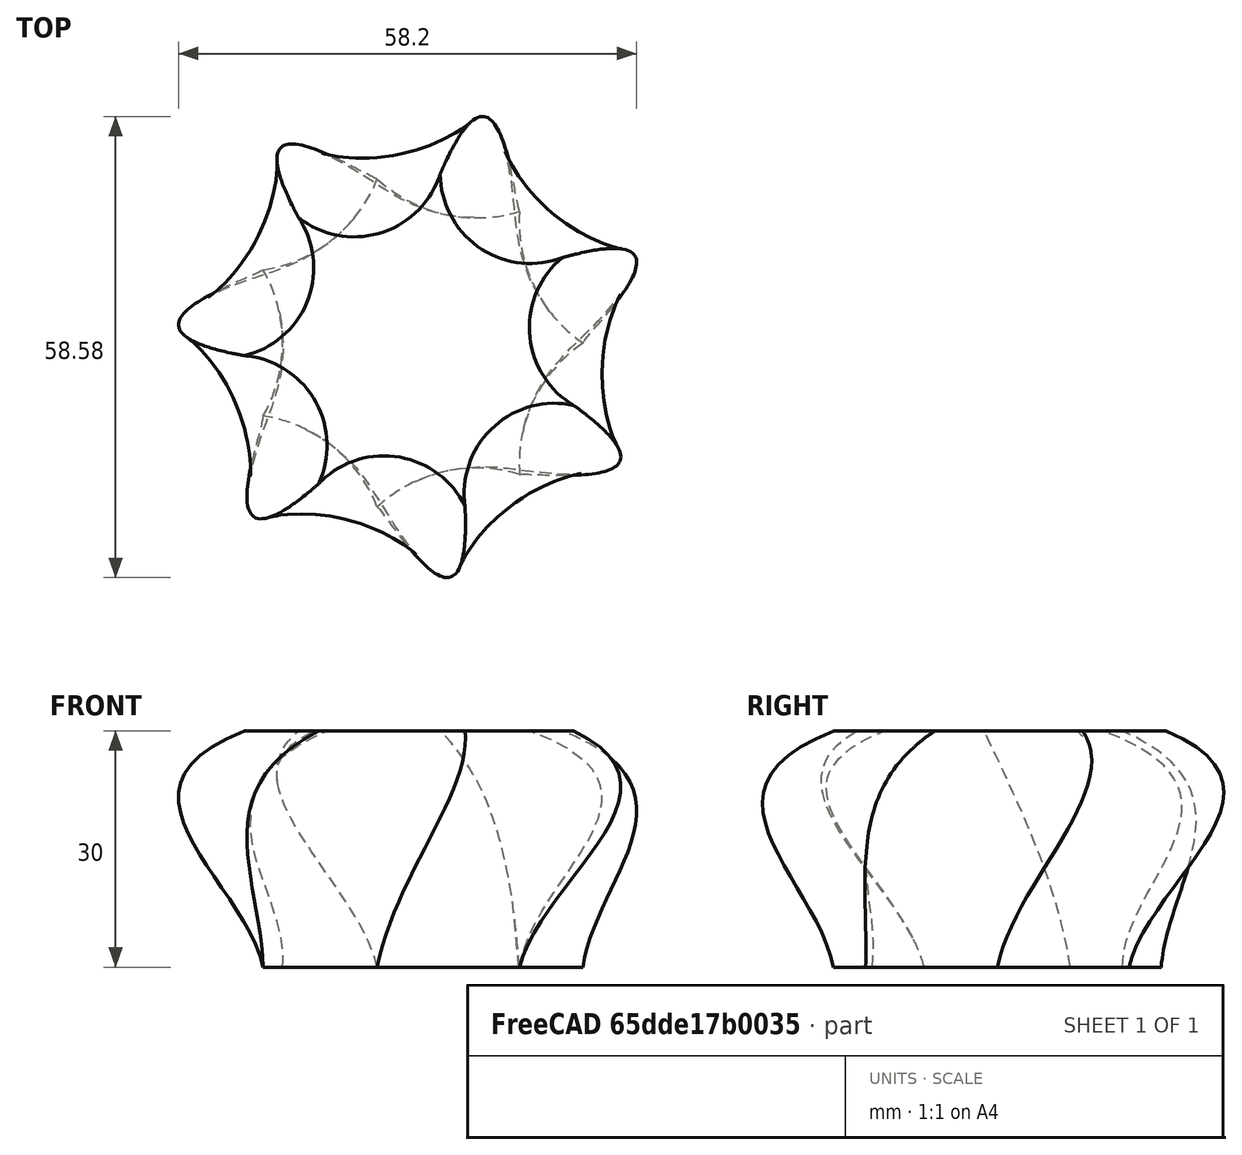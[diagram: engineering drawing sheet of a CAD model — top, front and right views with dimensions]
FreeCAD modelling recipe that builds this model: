
FCSTD DOCUMENT  (FreeCAD 1.2R20251119 (Git shallow))
Label: turned_loft
License: All rights reserved
LicenseURL: https://en.wikipedia.org/wiki/All_rights_reserved
objects: Sketcher::SketchObject×4, App::Point×1, PartDesign::AdditiveLoft×1, PartDesign::Body×1
note: 12 computed .brp shape members not serialized (recipe doc carries the construction recipe); baked Part::Feature solids carry a one-line shape summary decoded from their .brp

FEATURE [App::Point] Origin001
  Role = Origin
FEATURE [Sketcher::SketchObject] Sketch
  ArcFitTolerance = 1e-06
  AttachmentSupport = -> [Origin]
  ExternalTypes = [0]
  FullyConstrained = false
  MakeInternals = false
  MapMode = 5
  sketch-geometry (9):
    g0: ArcOfCircle CenterX=31.9361 CenterY=15.3796 CenterZ=0 NormalX=0 NormalY=0 NormalZ=1 AngleXU=0 Radius=18.6618 StartAngle=3.07054 EndAngle=4.11025
    g1: ArcOfCircle CenterX=31.9361 CenterY=-15.3796 CenterZ=0 NormalX=0 NormalY=0 NormalZ=1 AngleXU=0 Radius=18.6618 StartAngle=2.17294 EndAngle=3.21265
    g2: ArcOfCircle CenterX=7.88755 CenterY=-34.5576 CenterZ=0 NormalX=0 NormalY=0 NormalZ=1 AngleXU=0 Radius=18.6618 StartAngle=1.27534 EndAngle=2.31505
    g3: ArcOfCircle CenterX=-22.1004 CenterY=-27.7131 CenterZ=0 NormalX=0 NormalY=0 NormalZ=1 AngleXU=0 Radius=18.6618 StartAngle=0.377744 EndAngle=1.41745
    g4: ArcOfCircle CenterX=-35.4463 CenterY=2e-15 CenterZ=0 NormalX=0 NormalY=0 NormalZ=1 AngleXU=0 Radius=18.6618 StartAngle=5.76333 EndAngle=6.80304
    g5: ArcOfCircle CenterX=-22.1004 CenterY=27.7131 CenterZ=0 NormalX=0 NormalY=0 NormalZ=1 AngleXU=0 Radius=18.6618 StartAngle=4.86573 EndAngle=5.90544
    g6: ArcOfCircle CenterX=7.88755 CenterY=34.5576 CenterZ=0 NormalX=0 NormalY=0 NormalZ=1 AngleXU=0 Radius=18.6618 StartAngle=3.96814 EndAngle=5.00784
    g7: Circle [constr] CenterX=0 CenterY=0 CenterZ=0 NormalX=0 NormalY=0 NormalZ=1 AngleXU=0 Radius=35.4463
    g8: Circle [constr] CenterX=0 CenterY=0 CenterZ=0 NormalX=0 NormalY=0 NormalZ=1 AngleXU=0 Radius=21.3658
  constraints (30):
    c: Coincident(g3,g2)
    c: Coincident(g0,g6)
    c: Coincident(g7,g-1)
    c: PointOnObject(g6,g7)
    c: Coincident(g5,g6)
    c: PointOnObject(g0,g7)
    c: Coincident(g1,g0)
    c: PointOnObject(g1,g7)
    c: Coincident(g1,g2)
    c: PointOnObject(g2,g7)
    c: Equal(g2,g1)
    c: Equal(g1,g0)
    c: Coincident(g4,g5)
    c: Coincident(g3,g4)
    c: PointOnObject(g3,g7)
    c: PointOnObject(g4,g7)
    c: PointOnObject(g5,g7)
    c: Equal(g6,g5)
    c: Equal(g5,g4)
    c: Equal(g4,g3)
    c: Equal(g3,g2)
    c: Coincident(g8,g7)
    c: PointOnObject(g0,g8)
    c: PointOnObject(g5,g8)
    c: PointOnObject(g4,g8)
    c: PointOnObject(g3,g8)
    c: PointOnObject(g2,g8)
    c: PointOnObject(g1,g8)
    c: PointOnObject(g0,g8)
    c: PointOnObject(g0,g-1)
FEATURE [Sketcher::SketchObject] Sketch001
  ArcFitTolerance = 1e-06
  AttachmentOffset = pos=(0,0,10) rot=(0,0,1;0rad)
  AttachmentSupport = -> [Sketch]
  ExternalTypes = [0]
  FullyConstrained = false
  MakeInternals = false
  MapMode = 2
  Placement = pos=(0,0,10) rot=(0,0,1;0rad)
  sketch-geometry (10):
    g0: ArcOfCircle CenterX=31.7447 CenterY=22.8229 CenterZ=0 NormalX=0 NormalY=0 NormalZ=1 AngleXU=0 Radius=19.6047 StartAngle=3.168 EndAngle=4.36185
    g1: ArcOfCircle CenterX=37.6362 CenterY=-10.5892 CenterZ=0 NormalX=0 NormalY=0 NormalZ=1 AngleXU=0 Radius=19.6047 StartAngle=2.2704 EndAngle=3.46425
    g2: ArcOfCircle CenterX=15.1868 CenterY=-36.0274 CenterZ=0 NormalX=0 NormalY=0 NormalZ=1 AngleXU=0 Radius=19.6047 StartAngle=1.3728 EndAngle=2.56666
    g3: ArcOfCircle CenterX=-18.6985 CenterY=-34.3363 CenterZ=0 NormalX=0 NormalY=0 NormalZ=1 AngleXU=0 Radius=19.6047 StartAngle=0.475203 EndAngle=1.66906
    g4: ArcOfCircle CenterX=-38.5035 CenterY=-6.78921 CenterZ=0 NormalX=0 NormalY=0 NormalZ=1 AngleXU=0 Radius=19.6047 StartAngle=5.86079 EndAngle=7.05465
    g5: ArcOfCircle CenterX=-29.3146 CenterY=25.8703 CenterZ=0 NormalX=0 NormalY=0 NormalZ=1 AngleXU=0 Radius=19.6047 StartAngle=4.96319 EndAngle=6.15705
    g6: ArcOfCircle CenterX=1.94885 CenterY=39.0489 CenterZ=0 NormalX=0 NormalY=0 NormalZ=1 AngleXU=0 Radius=19.6047 StartAngle=4.06559 EndAngle=5.25945
    g7: Circle [constr] CenterX=0 CenterY=0 CenterZ=0 NormalX=0 NormalY=0 NormalZ=1 AngleXU=0 Radius=39.0975
    g8: Circle [constr] CenterX=0 CenterY=0 CenterZ=0 NormalX=0 NormalY=0 NormalZ=1 AngleXU=0 Radius=25.3983
    g9: LineSegment [constr] StartX=0 StartY=0 StartZ=0 EndX=25.0124 EndY=4.41037 EndZ=0
  constraints (32):
    c: Coincident(g3,g2)
    c: Coincident(g0,g6)
    c: Coincident(g7,g-1)
    c: PointOnObject(g6,g7)
    c: Coincident(g5,g6)
    c: PointOnObject(g0,g7)
    c: Coincident(g1,g0)
    c: PointOnObject(g1,g7)
    c: Coincident(g1,g2)
    c: PointOnObject(g2,g7)
    c: Equal(g2,g1)
    c: Equal(g1,g0)
    c: Coincident(g4,g5)
    c: Coincident(g3,g4)
    c: PointOnObject(g3,g7)
    c: PointOnObject(g4,g7)
    c: PointOnObject(g5,g7)
    c: Equal(g6,g5)
    c: Equal(g5,g4)
    c: Equal(g4,g3)
    c: Equal(g3,g2)
    c: Coincident(g8,g7)
    c: PointOnObject(g0,g8)
    c: PointOnObject(g5,g8)
    c: PointOnObject(g4,g8)
    c: PointOnObject(g3,g8)
    c: PointOnObject(g2,g8)
    c: PointOnObject(g1,g8)
    c: PointOnObject(g0,g8)
    c: Coincident(g9,g7)
    c: Coincident(g9,g0)
    c: Angle(g-1,g9) = 0.174533
FEATURE [Sketcher::SketchObject] Sketch002
  ArcFitTolerance = 1e-06
  AttachmentOffset = pos=(0,0,20) rot=(0,0,1;0rad)
  AttachmentSupport = -> [XY_Plane]
  ExternalTypes = [0]
  FullyConstrained = false
  MakeInternals = false
  MapMode = 2
  Placement = pos=(0,0,20) rot=(0,0,1;0rad)
  sketch-geometry (10):
    g0: ArcOfCircle CenterX=36.6006 CenterY=37.5248 CenterZ=0 NormalX=0 NormalY=0 NormalZ=1 AngleXU=0 Radius=28.5333 StartAngle=3.4658 EndAngle=4.41312
    g1: ArcOfCircle CenterX=52.1582 CenterY=-5.21921 CenterZ=0 NormalX=0 NormalY=0 NormalZ=1 AngleXU=0 Radius=28.5333 StartAngle=2.5682 EndAngle=3.51552
    g2: ArcOfCircle CenterX=28.4395 CenterY=-44.033 CenterZ=0 NormalX=0 NormalY=0 NormalZ=1 AngleXU=0 Radius=28.5333 StartAngle=1.6706 EndAngle=2.61792
    g3: ArcOfCircle CenterX=-16.6946 CenterY=-49.6891 CenterZ=0 NormalX=0 NormalY=0 NormalZ=1 AngleXU=0 Radius=28.5333 StartAngle=0.773004 EndAngle=1.72032
    g4: ArcOfCircle CenterX=-49.2574 CenterY=-17.9282 CenterZ=0 NormalX=0 NormalY=0 NormalZ=1 AngleXU=0 Radius=28.5333 StartAngle=6.15859 EndAngle=7.10591
    g5: ArcOfCircle CenterX=-44.7284 CenterY=27.3329 CenterZ=0 NormalX=0 NormalY=0 NormalZ=1 AngleXU=0 Radius=28.5333 StartAngle=5.26099 EndAngle=6.20831
    g6: ArcOfCircle CenterX=-6.51793 CenterY=52.0118 CenterZ=0 NormalX=0 NormalY=0 NormalZ=1 AngleXU=0 Radius=28.5333 StartAngle=4.3634 EndAngle=5.31071
    g7: Circle [constr] CenterX=0 CenterY=0 CenterZ=0 NormalX=0 NormalY=0 NormalZ=1 AngleXU=0 Radius=52.4187
    g8: Circle [constr] CenterX=0 CenterY=0 CenterZ=0 NormalX=0 NormalY=0 NormalZ=1 AngleXU=0 Radius=29.9974
    g9: LineSegment [constr] StartX=0 StartY=0 StartZ=0 EndX=28.1883 EndY=10.2597 EndZ=0
  constraints (32):
    c: Coincident(g3,g2)
    c: Coincident(g0,g6)
    c: Coincident(g7,g-1)
    c: PointOnObject(g6,g7)
    c: Coincident(g5,g6)
    c: PointOnObject(g0,g7)
    c: Coincident(g1,g0)
    c: PointOnObject(g1,g7)
    c: Coincident(g1,g2)
    c: PointOnObject(g2,g7)
    c: Equal(g2,g1)
    c: Equal(g1,g0)
    c: Coincident(g4,g5)
    c: Coincident(g3,g4)
    c: PointOnObject(g3,g7)
    c: PointOnObject(g4,g7)
    c: PointOnObject(g5,g7)
    c: Equal(g6,g5)
    c: Equal(g5,g4)
    c: Equal(g4,g3)
    c: Equal(g3,g2)
    c: Coincident(g8,g7)
    c: PointOnObject(g0,g8)
    c: PointOnObject(g5,g8)
    c: PointOnObject(g4,g8)
    c: PointOnObject(g3,g8)
    c: PointOnObject(g2,g8)
    c: PointOnObject(g1,g8)
    c: PointOnObject(g0,g8)
    c: Coincident(g9,g7)
    c: Coincident(g9,g0)
    c: Angle(g-1,g9) = 0.349066
FEATURE [Sketcher::SketchObject] Sketch003
  ArcFitTolerance = 1e-06
  AttachmentOffset = pos=(0,0,30) rot=(0,0,1;0rad)
  AttachmentSupport = -> [Origin]
  ExternalTypes = [0]
  FullyConstrained = false
  MakeInternals = false
  MapMode = 5
  Placement = pos=(0,0,30) rot=(0,0,1;0rad)
  sketch-geometry (10):
    g0: ArcOfCircle CenterX=14.7064 CenterY=21.5703 CenterZ=0 NormalX=0 NormalY=0 NormalZ=1 AngleXU=0 Radius=11.4747 StartAngle=3.15249 EndAngle=5.07549
    g1: ArcOfCircle CenterX=26.0337 CenterY=1.95095 CenterZ=0 NormalX=0 NormalY=0 NormalZ=1 AngleXU=0 Radius=11.4747 StartAngle=2.25489 EndAngle=4.17789
    g2: ArcOfCircle CenterX=17.7571 CenterY=-19.1375 CenterZ=0 NormalX=0 NormalY=0 NormalZ=1 AngleXU=0 Radius=11.4747 StartAngle=1.3573 EndAngle=3.28029
    g3: ArcOfCircle CenterX=-3.891 CenterY=-25.8151 CenterZ=0 NormalX=0 NormalY=0 NormalZ=1 AngleXU=0 Radius=11.4747 StartAngle=0.459699 EndAngle=2.38269
    g4: ArcOfCircle CenterX=-22.609 CenterY=-13.0533 CenterZ=0 NormalX=0 NormalY=0 NormalZ=1 AngleXU=0 Radius=11.4747 StartAngle=5.84529 EndAngle=7.76828
    g5: ArcOfCircle CenterX=-24.302 CenterY=9.53784 CenterZ=0 NormalX=0 NormalY=0 NormalZ=1 AngleXU=0 Radius=11.4747 StartAngle=4.94769 EndAngle=6.87068
    g6: ArcOfCircle CenterX=-7.69508 CenterY=24.9468 CenterZ=0 NormalX=0 NormalY=0 NormalZ=1 AngleXU=0 Radius=11.4747 StartAngle=4.05009 EndAngle=5.97309
    g7: Circle [constr] CenterX=0 CenterY=0 CenterZ=0 NormalX=0 NormalY=0 NormalZ=1 AngleXU=0 Radius=26.1067
    g8: Circle [constr] CenterX=0 CenterY=0 CenterZ=0 NormalX=0 NormalY=0 NormalZ=1 AngleXU=0 Radius=21.6875
    g9: LineSegment [constr] StartX=0 StartY=0 StartZ=0 EndX=18.7819 EndY=10.8438 EndZ=0
  constraints (32):
    c: Coincident(g3,g2)
    c: Coincident(g0,g6)
    c: Coincident(g7,g-1)
    c: PointOnObject(g6,g7)
    c: Coincident(g5,g6)
    c: PointOnObject(g0,g7)
    c: Coincident(g1,g0)
    c: PointOnObject(g1,g7)
    c: Coincident(g1,g2)
    c: PointOnObject(g2,g7)
    c: Equal(g2,g1)
    c: Equal(g1,g0)
    c: Coincident(g4,g5)
    c: Coincident(g3,g4)
    c: PointOnObject(g3,g7)
    c: PointOnObject(g4,g7)
    c: PointOnObject(g5,g7)
    c: Equal(g6,g5)
    c: Equal(g5,g4)
    c: Equal(g4,g3)
    c: Equal(g3,g2)
    c: Coincident(g8,g7)
    c: PointOnObject(g0,g8)
    c: PointOnObject(g5,g8)
    c: PointOnObject(g4,g8)
    c: PointOnObject(g3,g8)
    c: PointOnObject(g2,g8)
    c: PointOnObject(g1,g8)
    c: PointOnObject(g0,g8)
    c: Coincident(g9,g7)
    c: Coincident(g9,g0)
    c: Angle(g-1,g9) = 0.523599
FEATURE [PartDesign::AdditiveLoft] AdditiveLoft
  Closed = false
  Profile = -> Sketch
  Refine = true
  Ruled = false
  Sections = -> [Sketch001,Sketch002,Sketch003]
  Suppressed = false
FEATURE [PartDesign::Body] Body
  AllowCompound = false
  Group = -> [Sketch,Sketch001,Sketch002,AdditiveLoft,Sketch003]
  Origin = -> Origin
  Tip = -> AdditiveLoft
